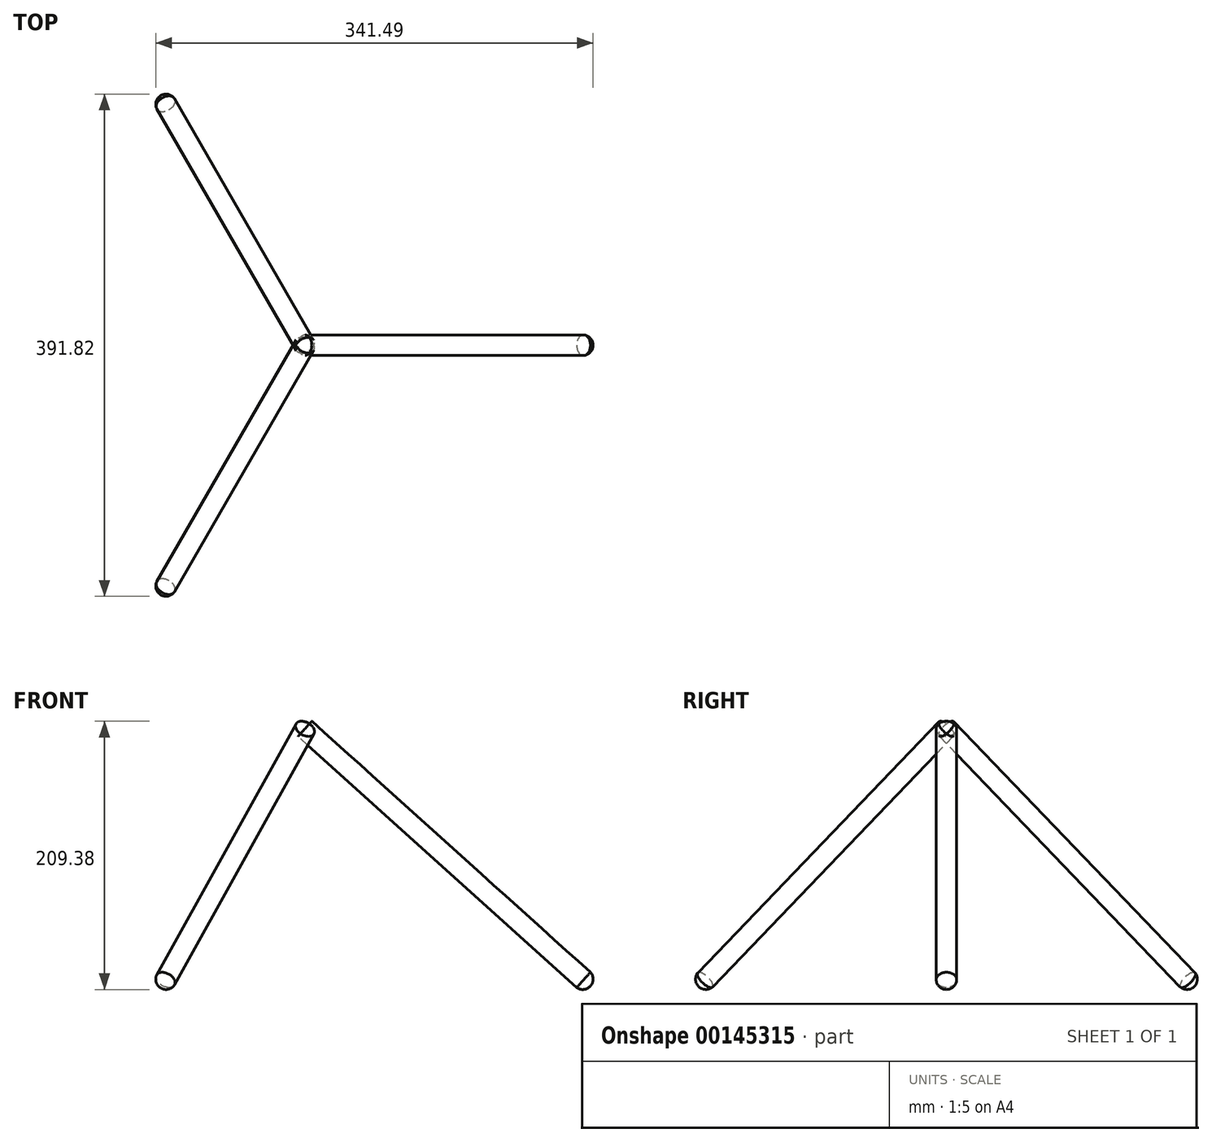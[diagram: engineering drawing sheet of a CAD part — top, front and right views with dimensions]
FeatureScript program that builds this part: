
annotation { "Feature Type Name" : "Feature", "Feature Type Description" : "" }
export const myFeature = defineFeature(function(context is Context, id is Id, definition is map)
    precondition{}
    {
        {
            var Q0;
            Q0=qCreatedBy(makeId("Front.planeOp"),FACE);
            var sketch = newSketch(context, id + "F0", { "sketchPlane" : qUnion([Q0])});
            skLineSegment(sketch, "E0", {"start": v(0, 0) * mm, "end": v(216.93, -195.4) * mm});
            skLineSegment(sketch, "E1.0", {"start": v(5.35, 5.94) * mm, "end": v(222.9, -190.01) * mm});
            skLineSegment(sketch, "E2", {"start": v(5.35, 5.94) * mm, "end": v(0, 0) * mm});
            skArc(sketch, "E3", {"start": v(222.9, -190.01) * mm, "mid": v(224.98, -195.4) * mm, "end": v(222.9, -200.78) * mm});
            skLineSegment(sketch, "E4", {"start": v(222.9, -200.78) * mm, "end": v(216.93, -195.4) * mm});
            skLineSegment(sketch, "E5", {"start": v(0, 44.4) * mm, "end": v(0, -36.72) * mm});
            skSolve(sketch);
        }
        {
            var Q0;
            Q0=makeQuery(id+"F0.imprint","IMPRINT",FACE,{"disambiguationData":[TD([[makeQuery(id+"F0.imprint","IMPRINT",EDGE,{"derivedFrom":sQuery(id+"F0.wireOp",EDGE,"E0")}),1.0]])]});
            var Q1;
            Q1=sQuery(id+"F0.wireOp",EDGE,"E0");
            revolve(context, id + "F1", {"entities" : qUnion([Q0]), "axis" : qUnion([Q1]), "revolveType" : RevolveType.FULL});
        }
        {
            var Q0;
            Q0=makeQuery(id+"F1.opRevolve","SWEPT_BODY",BODY,{"disambiguationData":[OSD([sQuery(id+"F0.wireOp",EDGE,"E0"),sQuery(id+"F0.wireOp",EDGE,"E1.0"),sQuery(id+"F0.wireOp",EDGE,"E2"),sQuery(id+"F0.wireOp",EDGE,"E3"),sQuery(id+"F0.wireOp",EDGE,"E4")])]});
            var Q1;
            Q1=sQuery(id+"F0.wireOp",EDGE,"E5");
            transform(context, id + "F2", {"entities" : qUnion([Q0]), "transformType" : TransformType.ROTATION, "transformAxis" : qUnion([Q1]), "angle" : 120 * degree, "makeCopy" : true});
        }
        {
            var Q0;
            Q0=makeQuery(id+"F1.opRevolve","SWEPT_BODY",BODY,{"disambiguationData":[OSD([sQuery(id+"F0.wireOp",EDGE,"E0"),sQuery(id+"F0.wireOp",EDGE,"E1.0"),sQuery(id+"F0.wireOp",EDGE,"E2"),sQuery(id+"F0.wireOp",EDGE,"E3"),sQuery(id+"F0.wireOp",EDGE,"E4")])]});
            var Q1;
            Q1=sQuery(id+"F0.wireOp",EDGE,"E5");
            transform(context, id + "F3", {"entities" : qUnion([Q0]), "transformType" : TransformType.ROTATION, "transformAxis" : qUnion([Q1]), "angle" : 240 * degree, "makeCopy" : true});
        }
    });
